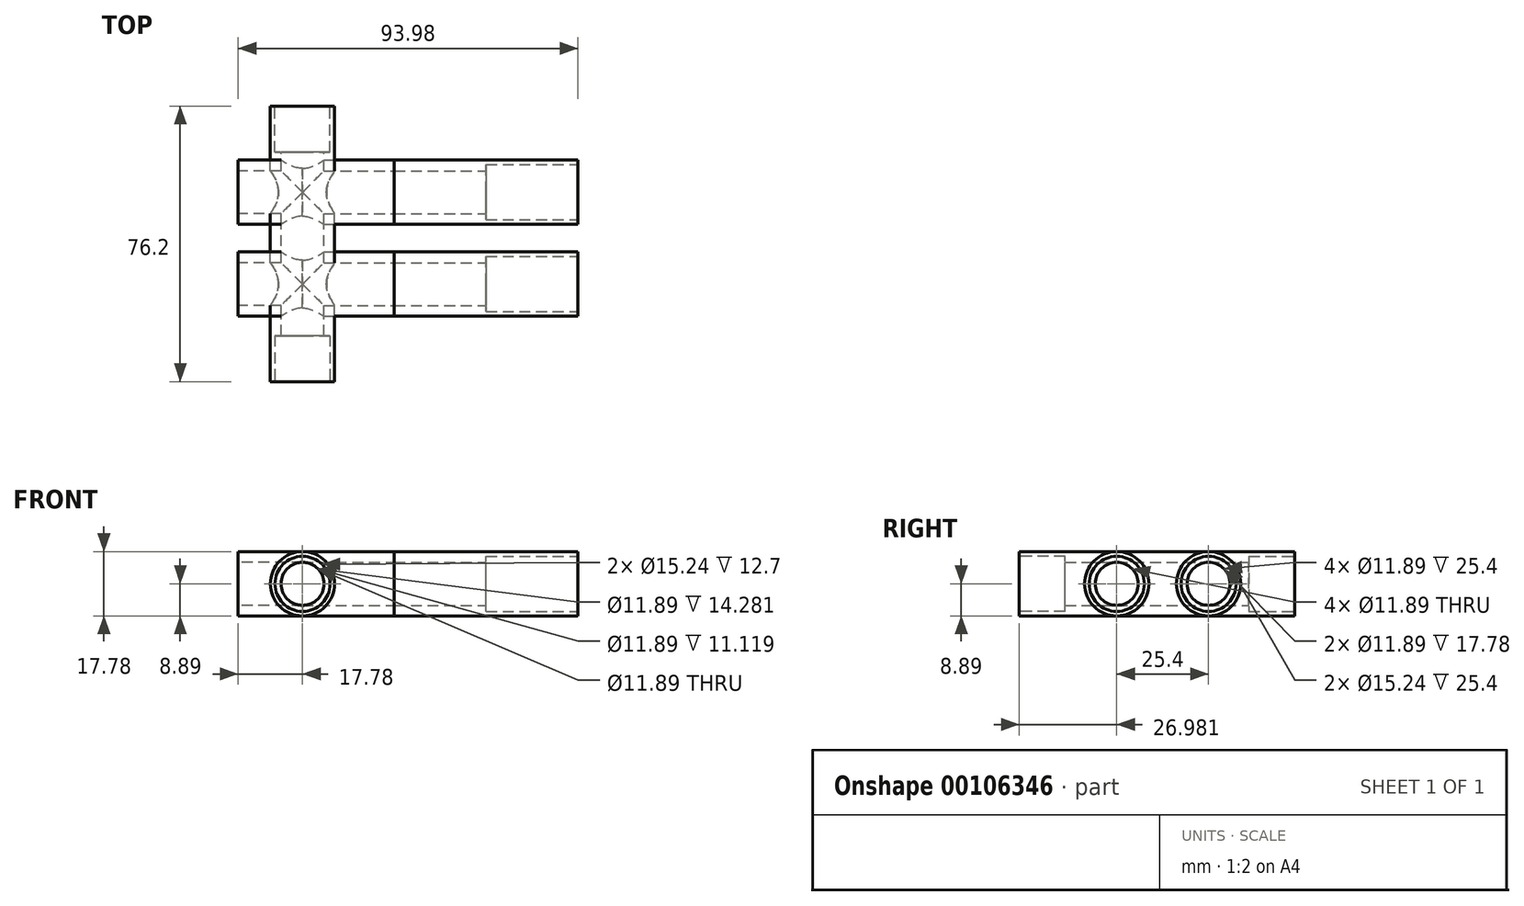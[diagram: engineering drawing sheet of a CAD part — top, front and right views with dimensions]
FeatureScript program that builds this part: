
annotation { "Feature Type Name" : "Feature", "Feature Type Description" : "" }
export const myFeature = defineFeature(function(context is Context, id is Id, definition is map)
    precondition{}
    {
        {
            var Q0;
            Q0=qCreatedBy(makeId("Front.planeOp"),FACE);
            var sketch = newSketch(context, id + "F0", { "sketchPlane" : qUnion([Q0])});
            skCircle(sketch, "E0", {"center": v(0, 0) * mm, "radius": 5.94 * mm});
            skCircle(sketch, "E1", {"center": v(0, 0) * mm, "radius": 8.9 * mm});
            skSolve(sketch);
        }
        {
            var Q0;
            Q0=qCreatedBy(makeId("Top.planeOp"),FACE);
            var sketch = newSketch(context, id + "F1", { "sketchPlane" : qUnion([Q0])});
            skLineSegment(sketch, "E2", {"start": v(0, 0) * mm, "end": v(0, 50.8) * mm});
            skSolve(sketch);
        }
        {
            var Q0;
            Q0=qCreatedBy(makeId("Right.planeOp"),FACE);
            var sketch = newSketch(context, id + "F2", { "sketchPlane" : qUnion([Q0])});
            skCircle(sketch, "E3", {"center": v(14.28, 0) * mm, "radius": 5.94 * mm});
            skCircle(sketch, "E4", {"center": v(39.68, 0) * mm, "radius": 5.94 * mm});
            skCircle(sketch, "E5", {"center": v(14.28, 0) * mm, "radius": 8.9 * mm});
            skCircle(sketch, "E6", {"center": v(39.68, 0) * mm, "radius": 8.9 * mm});
            skLineSegment(sketch, "E7", {"start": v(14.28, 0) * mm, "end": v(39.68, 0) * mm});
            skSolve(sketch);
        }
        {
            var Q0;
            Q0=qCreatedBy(makeId("Top.planeOp"),FACE);
            var sketch = newSketch(context, id + "F3", { "sketchPlane" : qUnion([Q0])});
            skLineSegment(sketch, "E8", {"start": v(0, 14.28) * mm, "end": v(25.4, 14.28) * mm});
            skLineSegment(sketch, "E9", {"start": v(0, 14.28) * mm, "end": v(-17.78, 14.28) * mm});
            skLineSegment(sketch, "E10", {"start": v(0, 39.68) * mm, "end": v(25.4, 39.68) * mm});
            skLineSegment(sketch, "E11", {"start": v(0, 39.68) * mm, "end": v(-17.78, 39.68) * mm});
            skSolve(sketch);
        }
        {
            var Q0;
            Q0=makeQuery(id+"F0.imprint","IMPRINT",FACE,{"disambiguationData":[TD([[makeQuery(id+"F0.imprint","IMPRINT",EDGE,{"derivedFrom":sQuery(id+"F0.wireOp",EDGE,"E0")}),-1.0]])]});
            var Q1;
            Q1=sQuery(id+"F1.wireOp",EDGE,"E2");
            sweep(context, id + "F4", {"profiles" : qUnion([Q0]), "path" : qUnion([Q1])});
        }
        {
            var Q0;
            Q0=makeQuery(id+"F2.imprint","IMPRINT",FACE,{"disambiguationData":[TD([[makeQuery(id+"F2.imprint","IMPRINT",EDGE,{"derivedFrom":sQuery(id+"F2.wireOp",EDGE,"E3")}),-1.0]])]});
            var Q1;
            Q1=makeQuery(id+"F2.imprint","IMPRINT",FACE,{"disambiguationData":[TD([[makeQuery(id+"F2.imprint","IMPRINT",EDGE,{"derivedFrom":sQuery(id+"F2.wireOp",EDGE,"E4")}),-1.0]])]});
            var Q2;
            Q2=sQuery(id+"F3.wireOp",EDGE,"E10");
            sweep(context, id + "F5", {"profiles" : qUnion([Q0, Q1]), "path" : qUnion([Q2])});
        }
        {
            var Q0;
            Q0=makeQuery(id+"F2.imprint","IMPRINT",FACE,{"disambiguationData":[TD([[makeQuery(id+"F2.imprint","IMPRINT",EDGE,{"derivedFrom":sQuery(id+"F2.wireOp",EDGE,"E4")}),-1.0]])]});
            var Q1;
            Q1=makeQuery(id+"F2.imprint","IMPRINT",FACE,{"disambiguationData":[TD([[makeQuery(id+"F2.imprint","IMPRINT",EDGE,{"derivedFrom":sQuery(id+"F2.wireOp",EDGE,"E3")}),-1.0]])]});
            var Q2;
            Q2=sQuery(id+"F3.wireOp",EDGE,"E11");
            sweep(context, id + "F6", {"profiles" : qUnion([Q0, Q1]), "path" : qUnion([Q2])});
        }
        {
            var Q0;
            Q0=makeQuery(id+"F2.imprint","IMPRINT",FACE,{"disambiguationData":[TD([[makeQuery(id+"F2.imprint","IMPRINT",EDGE,{"derivedFrom":sQuery(id+"F2.wireOp",EDGE,"E4")}),1.0]])]});
            var Q1;
            Q1=makeQuery(id+"F2.imprint","IMPRINT",FACE,{"disambiguationData":[TD([[makeQuery(id+"F2.imprint","IMPRINT",EDGE,{"derivedFrom":sQuery(id+"F2.wireOp",EDGE,"E3")}),1.0]])]});
            var Q2;
            Q2=sQuery(id+"F3.wireOp",EDGE,"E10");
            sweep(context, id + "F7", {"operationType" : NewBodyOperationType.REMOVE, "profiles" : qUnion([Q0, Q1]), "path" : qUnion([Q2])});
        }
        {
            var Q0;
            Q0=makeQuery(id+"F2.imprint","IMPRINT",FACE,{"disambiguationData":[TD([[makeQuery(id+"F2.imprint","IMPRINT",EDGE,{"derivedFrom":sQuery(id+"F2.wireOp",EDGE,"E4")}),1.0]])]});
            var Q1;
            Q1=makeQuery(id+"F2.imprint","IMPRINT",FACE,{"disambiguationData":[TD([[makeQuery(id+"F2.imprint","IMPRINT",EDGE,{"derivedFrom":sQuery(id+"F2.wireOp",EDGE,"E3")}),1.0]])]});
            var Q2;
            Q2=sQuery(id+"F3.wireOp",EDGE,"E11");
            sweep(context, id + "F8", {"operationType" : NewBodyOperationType.REMOVE, "profiles" : qUnion([Q0, Q1]), "path" : qUnion([Q2])});
        }
        {
            var Q0;
            Q0=makeQuery(id+"F0.imprint","IMPRINT",FACE,{"disambiguationData":[TD([[makeQuery(id+"F0.imprint","IMPRINT",EDGE,{"derivedFrom":sQuery(id+"F0.wireOp",EDGE,"E0")}),1.0]])]});
            var Q1;
            Q1=sQuery(id+"F1.wireOp",EDGE,"E2");
            sweep(context, id + "F9", {"operationType" : NewBodyOperationType.REMOVE, "profiles" : qUnion([Q0]), "path" : qUnion([Q1])});
        }
        {
            var Q0;
            Q0=qCreatedBy(makeId("Top.planeOp"),FACE);
            var sketch = newSketch(context, id + "F10", { "sketchPlane" : qUnion([Q0])});
            skLineSegment(sketch, "E12", {"start": v(25.4, 14.28) * mm, "end": v(76.2, 14.28) * mm});
            skLineSegment(sketch, "E13", {"start": v(25.4, 39.68) * mm, "end": v(76.2, 39.68) * mm});
            skArc(sketch, "E14", {"start": v(76.2, 14.28) * mm, "mid": v(146.9, -56.41) * mm, "end": v(76.2, -127.1) * mm});
            skArc(sketch, "E15", {"start": v(76.2, -127.1) * mm, "mid": v(29, -124.5) * mm, "end": v(-17.62, -116.71) * mm});
            skArc(sketch, "E16", {"start": v(-17.62, -116.71) * mm, "mid": v(-122.03, -43.57) * mm, "end": v(-144.76, 81.88) * mm});
            skLineSegment(sketch, "E17", {"start": v(-144.76, 81.88) * mm, "end": v(-118.94, 202.4) * mm});
            skArc(sketch, "E18", {"start": v(-118.94, 202.4) * mm, "mid": v(-78.29, 228.71) * mm, "end": v(-51.98, 188.06) * mm});
            skLineSegment(sketch, "E19", {"start": v(-51.98, 188.06) * mm, "end": v(-73, 89.93) * mm});
            skArc(sketch, "E20", {"start": v(-73, 89.93) * mm, "mid": v(-68.32, 73.37) * mm, "end": v(-52, 67.92) * mm});
            skLineSegment(sketch, "E21", {"start": v(-52, 67.92) * mm, "end": v(135.08, 67.92) * mm});
            skArc(sketch, "E22", {"start": v(135.08, 67.92) * mm, "mid": v(149.1, 53.89) * mm, "end": v(135.08, 39.86) * mm});
            skLineSegment(sketch, "E23", {"start": v(76.2, 39.68) * mm, "end": v(135.08, 39.86) * mm});
            skSolve(sketch);
        }
        {
            var Q0;
            Q0=makeQuery(id+"F0.imprint","IMPRINT",FACE,{"disambiguationData":[TD([[makeQuery(id+"F0.imprint","IMPRINT",EDGE,{"derivedFrom":sQuery(id+"F0.wireOp",EDGE,"E0")}),-1.0]])]});
            extrude(context, id + "F11", {"entities" : qUnion([Q0]), "operationType" : NewBodyOperationType.ADD, "depth" : 12.7 * mm});
        }
        {
            var Q0;
            Q0=makeQuery(id+"F4.opSweep","CAP_FACE",FACE,{"disambiguationData":[OSD([sQuery(id+"F0.wireOp",EDGE,"E0"),sQuery(id+"F0.wireOp",EDGE,"E1"),sQuery(id+"F1.wireOp",VERTEX,"E2.end")])],"isStart":false});
            extrude(context, id + "F12", {"entities" : qUnion([Q0]), "operationType" : NewBodyOperationType.ADD, "depth" : 12.7 * mm});
        }
        {
            var Q0;
            Q0=makeQuery(id+"F5.opSweep","CAP_FACE",FACE,{"disambiguationData":[OSD([sQuery(id+"F2.wireOp",EDGE,"E3"),sQuery(id+"F2.wireOp",EDGE,"E5"),sQuery(id+"F3.wireOp",VERTEX,"E10.end")])],"isStart":false});
            var Q1;
            Q1=makeQuery(id+"F5.opSweep","CAP_FACE",FACE,{"disambiguationData":[OSD([sQuery(id+"F2.wireOp",EDGE,"E4"),sQuery(id+"F2.wireOp",EDGE,"E6"),sQuery(id+"F3.wireOp",VERTEX,"E10.end")])],"isStart":false});
            var Q2;
            Q2=sQuery(id+"F10.wireOp",EDGE,"E12");
            sweep(context, id + "F13", {"profiles" : qUnion([Q0, Q1]), "path" : qUnion([Q2])});
        }
        {
            var Q0;
            Q0=makeQuery(id+"F13.opSweep","CAP_FACE",FACE,{"disambiguationData":[OSD([sQuery(id+"F2.wireOp",EDGE,"E3"),sQuery(id+"F2.wireOp",EDGE,"E5"),sQuery(id+"F3.wireOp",VERTEX,"E10.end"),sQuery(id+"F10.wireOp",VERTEX,"E12.end")])],"isStart":false});
            var sketch = newSketch(context, id + "F14", { "sketchPlane" : qUnion([Q0])});
            skCircle(sketch, "E24", {"center": v(14.28, 0) * mm, "radius": 7.62 * mm});
            skCircle(sketch, "E25", {"center": v(39.68, 0) * mm, "radius": 7.62 * mm});
            skSolve(sketch);
        }
        {
            var Q0;
            Q0=makeQuery(id+"F14.imprint","IMPRINT",FACE,{"disambiguationData":[TD([[makeQuery(id+"F14.imprint","IMPRINT",EDGE,{"derivedFrom":sQuery(id+"F14.wireOp",EDGE,"E24")}),1.0]])]});
            var Q1;
            Q1=makeQuery(id+"F14.imprint","IMPRINT",FACE,{"disambiguationData":[TD([[makeQuery(id+"F14.imprint","IMPRINT",EDGE,{"derivedFrom":sQuery(id+"F14.wireOp",EDGE,"E25")}),1.0]])]});
            extrude(context, id + "F15", {"entities" : qUnion([Q0, Q1]), "operationType" : NewBodyOperationType.REMOVE, "oppositeDirection" : true, "depth" : 25.4 * mm});
        }
        {
            var Q0;
            Q0=makeQuery(id+"F11.opExtrude","CAP_FACE",FACE,{"disambiguationData":[OSD([sQuery(id+"F0.wireOp",EDGE,"E0"),sQuery(id+"F0.wireOp",EDGE,"E1")])],"isStart":false});
            var sketch = newSketch(context, id + "F16", { "sketchPlane" : qUnion([Q0])});
            skCircle(sketch, "E26", {"center": v(0, 0) * mm, "radius": 7.62 * mm});
            skSolve(sketch);
        }
        {
            var Q0;
            Q0=makeQuery(id+"F12.opExtrude","CAP_FACE",FACE,{"disambiguationData":[OSD([sQuery(id+"F0.wireOp",EDGE,"E0"),sQuery(id+"F0.wireOp",EDGE,"E1"),sQuery(id+"F1.wireOp",VERTEX,"E2.end")])],"isStart":false});
            var sketch = newSketch(context, id + "F17", { "sketchPlane" : qUnion([Q0])});
            skCircle(sketch, "E27", {"center": v(0, 0) * mm, "radius": 7.62 * mm});
            skSolve(sketch);
        }
        {
            var Q0;
            Q0=makeQuery(id+"F17.imprint","IMPRINT",FACE,{"disambiguationData":[TD([[makeQuery(id+"F17.imprint","IMPRINT",EDGE,{"derivedFrom":sQuery(id+"F17.wireOp",EDGE,"E27")}),1.0]])]});
            extrude(context, id + "F18", {"entities" : qUnion([Q0]), "operationType" : NewBodyOperationType.REMOVE, "oppositeDirection" : true, "depth" : 12.7 * mm});
        }
        {
            var Q0;
            Q0=makeQuery(id+"F16.imprint","IMPRINT",FACE,{"disambiguationData":[TD([[makeQuery(id+"F16.imprint","IMPRINT",EDGE,{"derivedFrom":sQuery(id+"F16.wireOp",EDGE,"E26")}),1.0]])]});
            extrude(context, id + "F19", {"entities" : qUnion([Q0]), "operationType" : NewBodyOperationType.REMOVE, "oppositeDirection" : true, "depth" : 12.7 * mm});
        }
    });
